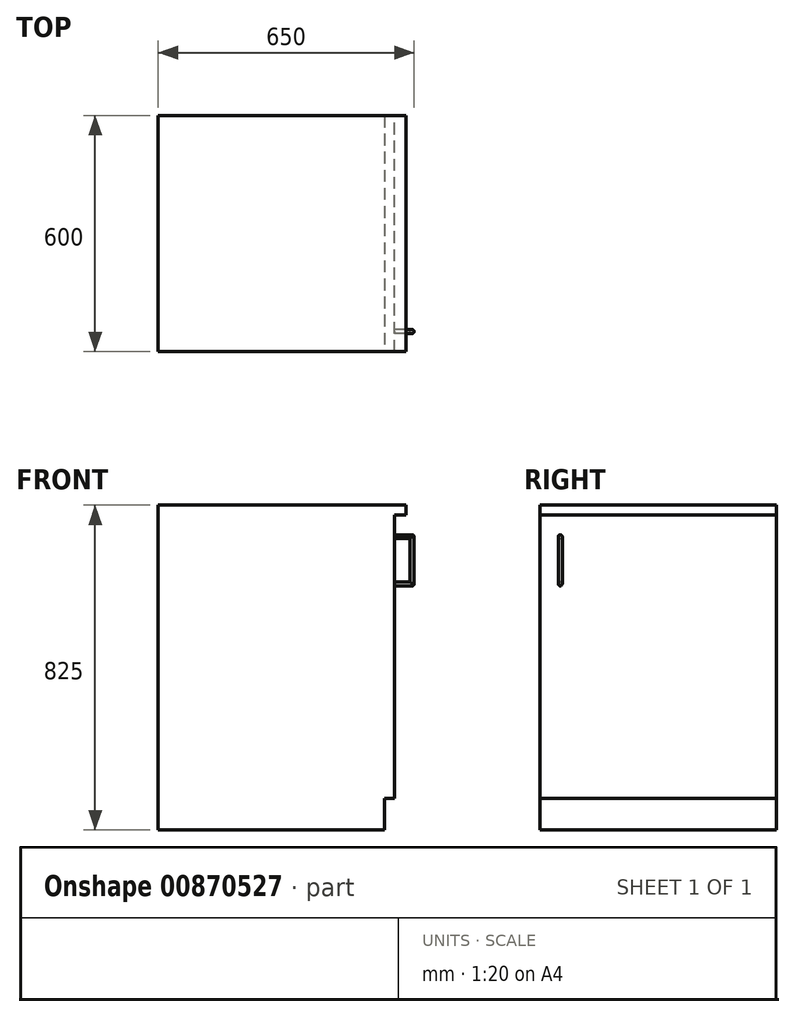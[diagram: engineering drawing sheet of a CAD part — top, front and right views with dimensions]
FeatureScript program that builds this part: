
annotation { "Feature Type Name" : "Feature", "Feature Type Description" : "" }
export const myFeature = defineFeature(function(context is Context, id is Id, definition is map)
    precondition{}
    {
        {
            var Q0;
            Q0=qCreatedBy(makeId("Top.planeOp"),FACE);
            var sketch = newSketch(context, id + "F0", { "sketchPlane" : qUnion([Q0])});
            skLineSegment(sketch, "E0.bottom", {"start": v(-300, 300) * mm, "end": v(300, 300) * mm});
            skLineSegment(sketch, "E0.top", {"start": v(-300, -300) * mm, "end": v(300, -300) * mm});
            skLineSegment(sketch, "E0.left", {"start": v(-300, 300) * mm, "end": v(-300, -300) * mm});
            skLineSegment(sketch, "E0.right", {"start": v(300, 300) * mm, "end": v(300, -300) * mm});
            skPoint(sketch, "E0.middle", {"position": v(0, 0) * mm});
            skSolve(sketch);
        }
        {
            var Q0;
            Q0 = qSketchRegion(id + "F0", true);
            extrude(context, id + "F1", {"entities" : qUnion([Q0]), "depth" : 800 * mm, "offsetDistance" : 25 * mm});
        }
        {
            var Q0;
            Q0=makeQuery(id+"F1.opExtrude","SWEPT_FACE",FACE,{"disambiguationData":[OSD([sQuery(id+"F0.wireOp",EDGE,"E0.right")])]});
            var sketch = newSketch(context, id + "F2", { "sketchPlane" : qUnion([Q0])});
            skLineSegment(sketch, "E1.bottom", {"start": v(-300, 0) * mm, "end": v(300, 0) * mm});
            skLineSegment(sketch, "E1.top", {"start": v(-300, 80) * mm, "end": v(300, 80) * mm});
            skLineSegment(sketch, "E1.left", {"start": v(-300, 0) * mm, "end": v(-300, 80) * mm});
            skLineSegment(sketch, "E1.right", {"start": v(300, 0) * mm, "end": v(300, 80) * mm});
            skSolve(sketch);
        }
        {
            var Q0;
            Q0 = qSketchRegion(id + "F2", true);
            extrude(context, id + "F3", {"entities" : qUnion([Q0]), "operationType" : NewBodyOperationType.REMOVE, "oppositeDirection" : true, "depth" : 25 * mm, "offsetDistance" : 25 * mm});
        }
        {
            var Q0;
            Q0=makeQuery(id+"F1.opExtrude","SWEPT_FACE",FACE,{"disambiguationData":[OSD([sQuery(id+"F0.wireOp",EDGE,"E0.right")])]});
            var sketch = newSketch(context, id + "F4", { "sketchPlane" : qUnion([Q0])});
            skLineSegment(sketch, "E2.bottom", {"start": v(-248.58, 750) * mm, "end": v(-248.58, 750) * mm});
            skLineSegment(sketch, "E2.top", {"start": v(-248.58, 620) * mm, "end": v(-248.58, 620) * mm});
            skLineSegment(sketch, "E2.left", {"start": v(-253.58, 745) * mm, "end": v(-253.58, 625) * mm});
            skLineSegment(sketch, "E2.right", {"start": v(-243.58, 745) * mm, "end": v(-243.58, 625) * mm});
            skPoint(sketch, "E3.visualSharp", {"position": v(-243.58, 750) * mm});
            skArc(sketch, "E3.filletArc", {"start": v(-243.58, 745) * mm, "mid": v(-245.04, 748.54) * mm, "end": v(-248.58, 750) * mm});
            skPoint(sketch, "E4.visualSharp", {"position": v(-243.58, 620) * mm});
            skArc(sketch, "E4.filletArc", {"start": v(-248.58, 620) * mm, "mid": v(-245.04, 621.46) * mm, "end": v(-243.58, 625) * mm});
            skPoint(sketch, "E5.visualSharp", {"position": v(-253.58, 620) * mm});
            skArc(sketch, "E5.filletArc", {"start": v(-253.58, 625) * mm, "mid": v(-252.12, 621.46) * mm, "end": v(-248.58, 620) * mm});
            skPoint(sketch, "E6.visualSharp", {"position": v(-253.58, 750) * mm});
            skArc(sketch, "E6.filletArc", {"start": v(-248.58, 750) * mm, "mid": v(-252.12, 748.54) * mm, "end": v(-253.58, 745) * mm});
            skSolve(sketch);
        }
        {
            var Q0;
            Q0 = qSketchRegion(id + "F4", true);
            extrude(context, id + "F5", {"entities" : qUnion([Q0]), "operationType" : NewBodyOperationType.ADD, "depth" : 50 * mm, "offsetDistance" : 25 * mm});
        }
        {
            var Q0;
            Q0=makeQuery(id+"F5.opExtrude","CAP_FACE",FACE,{"disambiguationData":[OSD([sQuery(id+"F4.wireOp",EDGE,"E2.left"),sQuery(id+"F4.wireOp",EDGE,"E2.right"),sQuery(id+"F4.wireOp",EDGE,"E3.filletArc"),sQuery(id+"F4.wireOp",EDGE,"E4.filletArc"),sQuery(id+"F4.wireOp",EDGE,"E5.filletArc"),sQuery(id+"F4.wireOp",EDGE,"E6.filletArc")])],"isStart":false});
            fillet(context, id + "F6", {"entities" : qUnion([Q0]), "radius" : 5 * mm, "tangentPropagation" : true, "allowEdgeOverflow" : false});
        }
        {
            var Q0;
            Q0=makeQuery(id+"F5.opExtrude","SWEPT_FACE",FACE,{"disambiguationData":[OSD([sQuery(id+"F4.wireOp",EDGE,"E2.right")])]});
            var sketch = newSketch(context, id + "F7", { "sketchPlane" : qUnion([Q0])});
            skLineSegment(sketch, "E7.bottom", {"start": v(-340, 740) * mm, "end": v(-300, 740) * mm});
            skLineSegment(sketch, "E7.top", {"start": v(-340, 630) * mm, "end": v(-300, 630) * mm});
            skLineSegment(sketch, "E7.left", {"start": v(-340, 740) * mm, "end": v(-340, 630) * mm});
            skLineSegment(sketch, "E7.right", {"start": v(-300, 740) * mm, "end": v(-300, 630) * mm});
            skSolve(sketch);
        }
        {
            var Q0;
            Q0=makeQuery(id+"F7.imprint","IMPRINT",FACE,{"disambiguationData":[TD([[makeQuery(id+"F7.imprint","IMPRINT",EDGE,{"derivedFrom":sQuery(id+"F7.wireOp",EDGE,"E7.bottom")}),-1.0]])]});
            extrude(context, id + "F8", {"entities" : qUnion([Q0]), "operationType" : NewBodyOperationType.REMOVE, "oppositeDirection" : true, "depth" : 25 * mm, "offsetDistance" : 25 * mm});
        }
        {
            var Q0;
            Q0=makeQuery(id+"F8.boolean.opBoolean","COPY",EDGE,{"derivedFrom":makeQuery(id+"F8.opExtrude","CAP_EDGE",EDGE,{"disambiguationData":[OSD([sQuery(id+"F7.wireOp",EDGE,"E7.bottom")])],"isStart":true})});
            var Q1;
            Q1=makeQuery(id+"F8.boolean.opBoolean","COPY",EDGE,{"derivedFrom":makeQuery(id+"F8.opExtrude","CAP_EDGE",EDGE,{"disambiguationData":[OSD([sQuery(id+"F7.wireOp",EDGE,"E7.left")])],"isStart":true})});
            var Q2;
            Q2=makeQuery(id+"F8.boolean.opBoolean","COPY",EDGE,{"derivedFrom":makeQuery(id+"F8.opExtrude","CAP_EDGE",EDGE,{"disambiguationData":[OSD([sQuery(id+"F7.wireOp",EDGE,"E7.top")])],"isStart":true})});
            var Q3;
            Q3=makeQuery(id+"F8.boolean.opBoolean","INTERSECT",EDGE,{"derivedFrom":[makeQuery(id+"F5.opExtrude","SWEPT_FACE",FACE,{"disambiguationData":[OSD([sQuery(id+"F4.wireOp",EDGE,"E2.left")])]}),makeQuery(id+"F8.opExtrude","SWEPT_FACE",FACE,{"disambiguationData":[OSD([sQuery(id+"F7.wireOp",EDGE,"E7.bottom")])]})]});
            var Q4;
            Q4=makeQuery(id+"F8.boolean.opBoolean","INTERSECT",EDGE,{"derivedFrom":[makeQuery(id+"F5.opExtrude","SWEPT_FACE",FACE,{"disambiguationData":[OSD([sQuery(id+"F4.wireOp",EDGE,"E2.left")])]}),makeQuery(id+"F8.opExtrude","SWEPT_FACE",FACE,{"disambiguationData":[OSD([sQuery(id+"F7.wireOp",EDGE,"E7.left")])]})]});
            var Q5;
            Q5=makeQuery(id+"F8.boolean.opBoolean","INTERSECT",EDGE,{"derivedFrom":[makeQuery(id+"F5.opExtrude","SWEPT_FACE",FACE,{"disambiguationData":[OSD([sQuery(id+"F4.wireOp",EDGE,"E2.left")])]}),makeQuery(id+"F8.opExtrude","SWEPT_FACE",FACE,{"disambiguationData":[OSD([sQuery(id+"F7.wireOp",EDGE,"E7.top")])]})]});
            fillet(context, id + "F9", {"entities" : qUnion([Q0, Q1, Q2, Q3, Q4, Q5]), "radius" : 5 * mm, "tangentPropagation" : true, "allowEdgeOverflow" : false});
        }
        {
            var Q0;
            Q0=makeQuery(id+"F1.opExtrude","CAP_FACE",FACE,{"disambiguationData":[OSD([sQuery(id+"F0.wireOp",EDGE,"E0.bottom"),sQuery(id+"F0.wireOp",EDGE,"E0.top"),sQuery(id+"F0.wireOp",EDGE,"E0.left"),sQuery(id+"F0.wireOp",EDGE,"E0.right")])],"isStart":false});
            var sketch = newSketch(context, id + "F10", { "sketchPlane" : qUnion([Q0])});
            skLineSegment(sketch, "E8.bottom", {"start": v(-300, -300) * mm, "end": v(330, -300) * mm});
            skLineSegment(sketch, "E8.top", {"start": v(-300, 300) * mm, "end": v(330, 300) * mm});
            skLineSegment(sketch, "E8.left", {"start": v(-300, -300) * mm, "end": v(-300, 300) * mm});
            skLineSegment(sketch, "E8.right", {"start": v(330, -300) * mm, "end": v(330, 300) * mm});
            skSolve(sketch);
        }
        {
            var Q0;
            Q0 = qSketchRegion(id + "F10", true);
            extrude(context, id + "F11", {"entities" : qUnion([Q0]), "operationType" : NewBodyOperationType.ADD, "depth" : 25 * mm, "offsetDistance" : 25 * mm});
        }
    });
